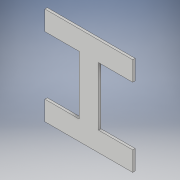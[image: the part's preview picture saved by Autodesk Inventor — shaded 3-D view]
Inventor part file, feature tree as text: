
AUTODESK INVENTOR PART (.ipt)
format: ipt  version: 2017 (Build 210142000, 142)  size: 146,432 bytes
history: native  units: in
note: dims shown in document units (in); Inventor stores cm internally (conversion verified against a paired STEP export)
features: extrude x4, sketch x4, thicken_offset x3
ambient origin geometry x8: Origin, YZ Plane, XZ Plane, XY Plane, X Axis, Y Axis, Z Axis, Center Point
bodies: Solid1 (feature_tree)
feature tree (11):
  extrude  "Extrusion1"  Depth=14.0in
  extrude  "Extrusion3"  Depth=0.25in TaperAngle=0.0deg
  thicken_offset  "Thicken1"
  thicken_offset  "Thicken2"
  thicken_offset  "Thicken3"
  extrude  "Extrusion4"  Depth=4.0in
  extrude  "Extrusion5"  Depth=3.5in
  sketch  "Sketch1"  dims[d0=2.0in d1=14.0in]
  sketch  "Sketch2"  dims[d2=0.25in d3=0.0in d6=0.25in d7=0.0in]
  sketch  "Sketch3"  dims[d8=4.0in d9=4.0in]
  sketch  "Sketch4"  dims[d10=3.5in d11=3.5in d12=3.5in d13=3.5in d14=3.5in d15=0.0in d16=3.5in d17=0.0in]
